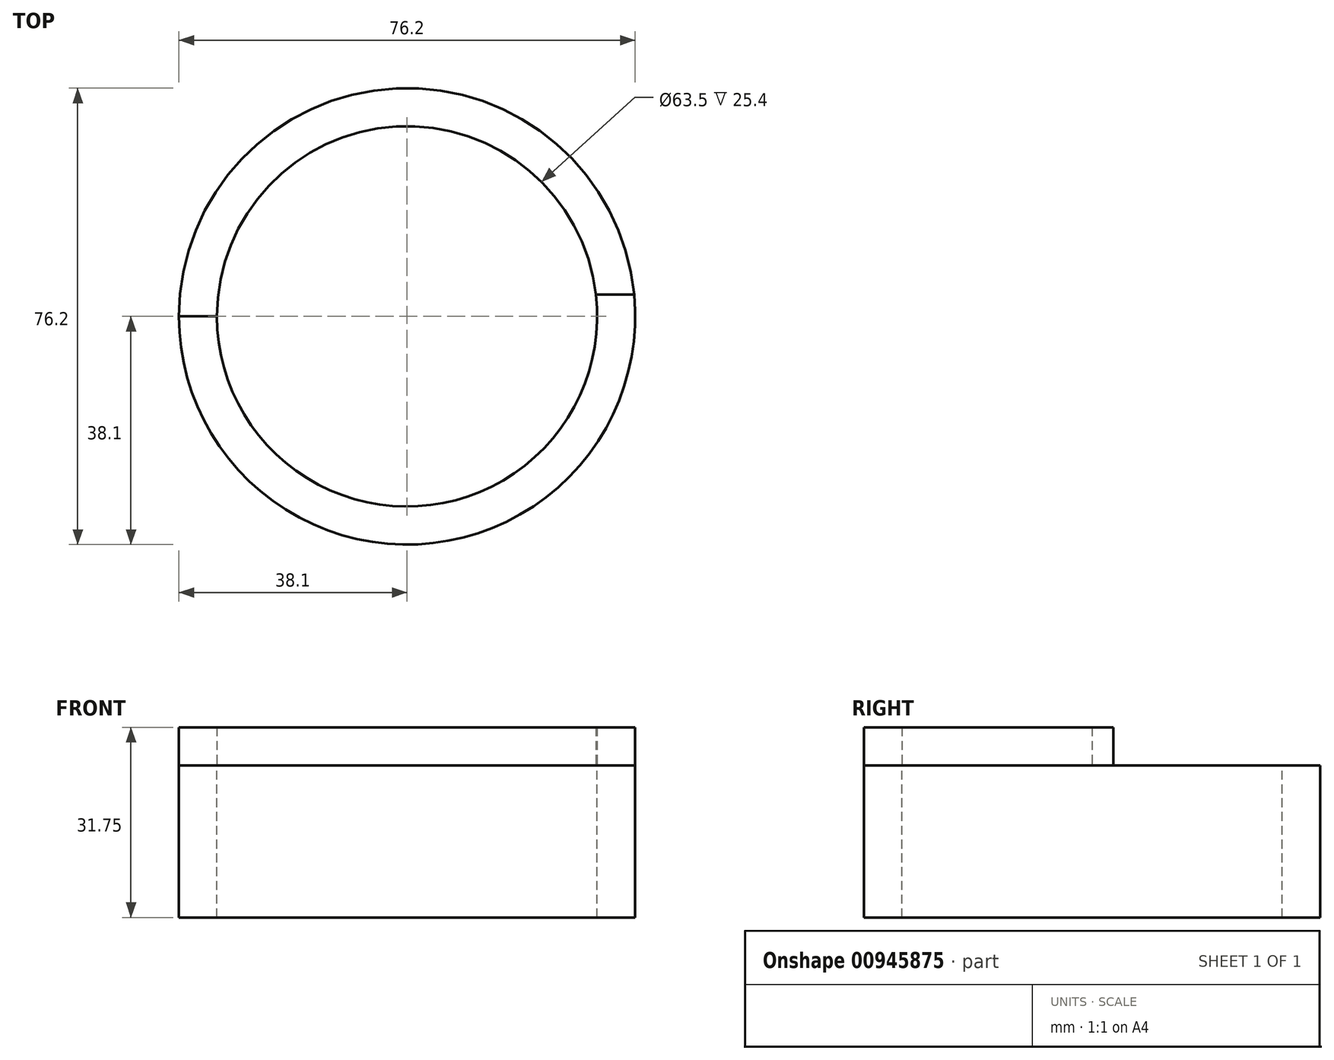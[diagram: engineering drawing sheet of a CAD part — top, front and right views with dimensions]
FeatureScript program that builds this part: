
annotation { "Feature Type Name" : "Feature", "Feature Type Description" : "" }
export const myFeature = defineFeature(function(context is Context, id is Id, definition is map)
    precondition{}
    {
        {
            var Q0;
            Q0=qCreatedBy(makeId("Top.planeOp"),FACE);
            var sketch = newSketch(context, id + "F0", { "sketchPlane" : qUnion([Q0])});
            skCircle(sketch, "E0", {"center": v(0, 0) * mm, "radius": 38.1 * mm});
            skCircle(sketch, "E1", {"center": v(0, 0) * mm, "radius": 31.75 * mm});
            skLineSegment(sketch, "E2", {"start": v(-38.1, 0) * mm, "end": v(38.1, 0) * mm});
            skLineSegment(sketch, "E3", {"start": v(-38.06, 3.61) * mm, "end": v(-31.54, 3.61) * mm});
            skLineSegment(sketch, "E4", {"start": v(-31.54, 3.61) * mm, "end": v(31.54, 3.61) * mm});
            skLineSegment(sketch, "E5", {"start": v(31.54, 3.61) * mm, "end": v(37.93, 3.61) * mm});
            skSolve(sketch);
        }
        {
            var Q0;
            {var subQ0=sQuery(id+"F0.wireOp",EDGE,"E2");var subQ1=sQuery(id+"F0.wireOp",EDGE,"E0");var subQ2=makeQuery(id+"F0.imprint","INTERSECT",VERTEX,{"disambiguationData":[OD(0.0)],"derivedFrom":[subQ1,subQ0]});Q0=makeQuery(id+"F0.imprint","IMPRINT",FACE,{"disambiguationData":[TD([[makeQuery(id+"F0.imprint","IMPRINT",EDGE,{"disambiguationData":[TD([[subQ2,1.0]])],"derivedFrom":subQ1}),1.0]])]});}
            var Q1;
            {var subQ3=sQuery(id+"F0.wireOp",EDGE,"E5");Q1=makeQuery(id+"F0.imprint","IMPRINT",FACE,{"disambiguationData":[TD([[makeQuery(id+"F0.imprint","IMPRINT",EDGE,{"derivedFrom":subQ3}),-1.0]])]});}
            extrude(context, id + "F1", {"entities" : qUnion([Q0, Q1]), "depth" : 6.35 * mm, "offsetDistance" : 25.4 * mm});
        }
        {
            var Q0;
            Q0 = qSketchRegion(id + "F0", true);
            extrude(context, id + "F2", {"entities" : qUnion([Q0]), "oppositeDirection" : true, "depth" : 25.4 * mm, "offsetDistance" : 25.4 * mm});
        }
    });
